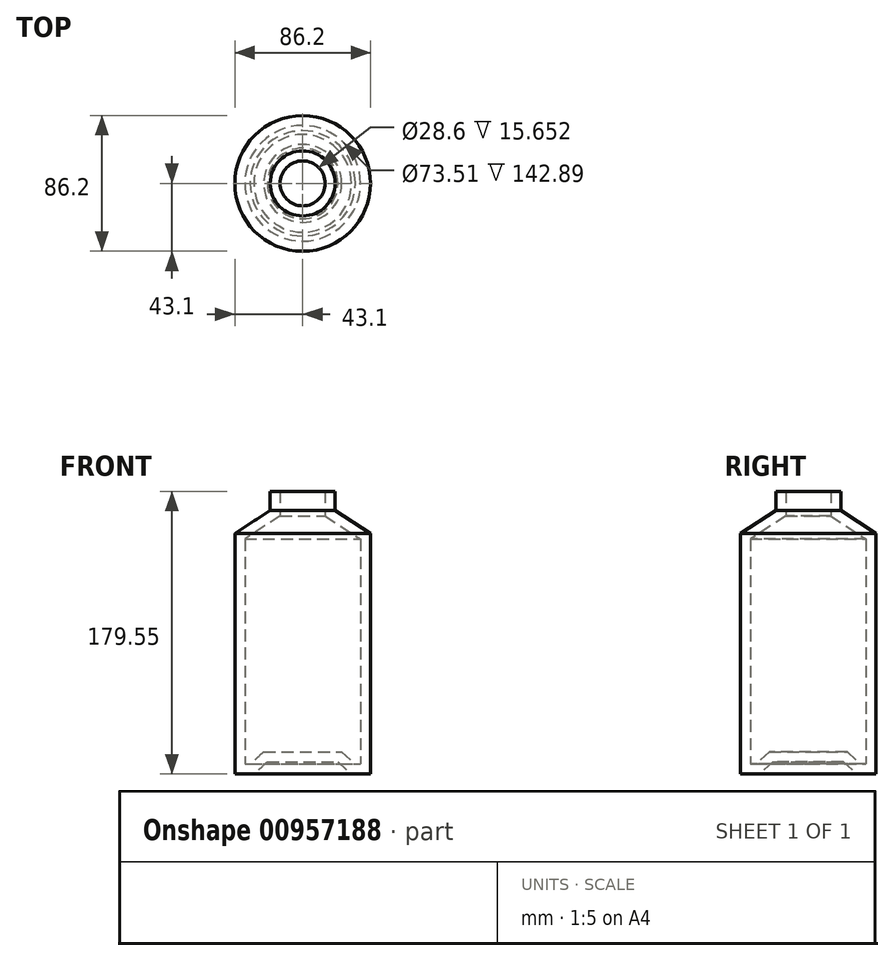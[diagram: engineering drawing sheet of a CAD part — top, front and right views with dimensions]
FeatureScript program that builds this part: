
annotation { "Feature Type Name" : "Feature", "Feature Type Description" : "" }
export const myFeature = defineFeature(function(context is Context, id is Id, definition is map)
    precondition{}
    {
        {
            var Q0;
            Q0=qCreatedBy(makeId("Front.planeOp"),FACE);
            var sketch = newSketch(context, id + "F0", { "sketchPlane" : qUnion([Q0])});
            skLineSegment(sketch, "E0", {"start": v(0, 0) * mm, "end": v(0, 75.08) * mm, "construction": true});
            skLineSegment(sketch, "E1", {"start": v(0, 0) * mm, "end": v(22.37, 0) * mm});
            skLineSegment(sketch, "E2", {"start": v(22.37, 0) * mm, "end": v(31.01, -7.63) * mm});
            skLineSegment(sketch, "E3", {"start": v(31.01, -7.63) * mm, "end": v(43.1, -7.63) * mm});
            skLineSegment(sketch, "E4", {"start": v(43.1, -7.63) * mm, "end": v(43.1, 145.05) * mm});
            skLineSegment(sketch, "E5", {"start": v(43.1, 145.05) * mm, "end": v(20.65, 159.7) * mm});
            skLineSegment(sketch, "E6", {"start": v(20.65, 159.7) * mm, "end": v(20.65, 171.92) * mm});
            skLineSegment(sketch, "E7.0", {"start": v(14.3, 156.27) * mm, "end": v(14.3, 171.92) * mm});
            skLineSegment(sketch, "E7.1", {"start": v(36.75, 141.61) * mm, "end": v(14.3, 156.27) * mm});
            skLineSegment(sketch, "E7.2", {"start": v(0, 6.35) * mm, "end": v(24.78, 6.35) * mm});
            skLineSegment(sketch, "E7.3", {"start": v(24.78, 6.35) * mm, "end": v(33.41, -1.28) * mm});
            skLineSegment(sketch, "E7.4", {"start": v(33.41, -1.28) * mm, "end": v(36.75, -1.28) * mm});
            skLineSegment(sketch, "E7.5", {"start": v(36.75, -1.28) * mm, "end": v(36.75, 141.61) * mm});
            skLineSegment(sketch, "E8", {"start": v(14.3, 171.92) * mm, "end": v(20.65, 171.92) * mm});
            skLineSegment(sketch, "E9", {"start": v(0, 0) * mm, "end": v(0, 6.35) * mm});
            skSolve(sketch);
        }
        {
            var Q0;
            Q0=makeQuery(id+"F0.imprint","IMPRINT",FACE,{"disambiguationData":[TD([[makeQuery(id+"F0.imprint","IMPRINT",EDGE,{"derivedFrom":sQuery(id+"F0.wireOp",EDGE,"E1")}),1.0]])]});
            var Q1;
            Q1=sQuery(id+"F0.wireOp",EDGE,"E0");
            revolve(context, id + "F1", {"surfaceOperationType" : NewSurfaceOperationType.NEW, "entities" : qUnion([Q0]), "axis" : qUnion([Q1]), "revolveType" : RevolveType.FULL});
        }
    });
